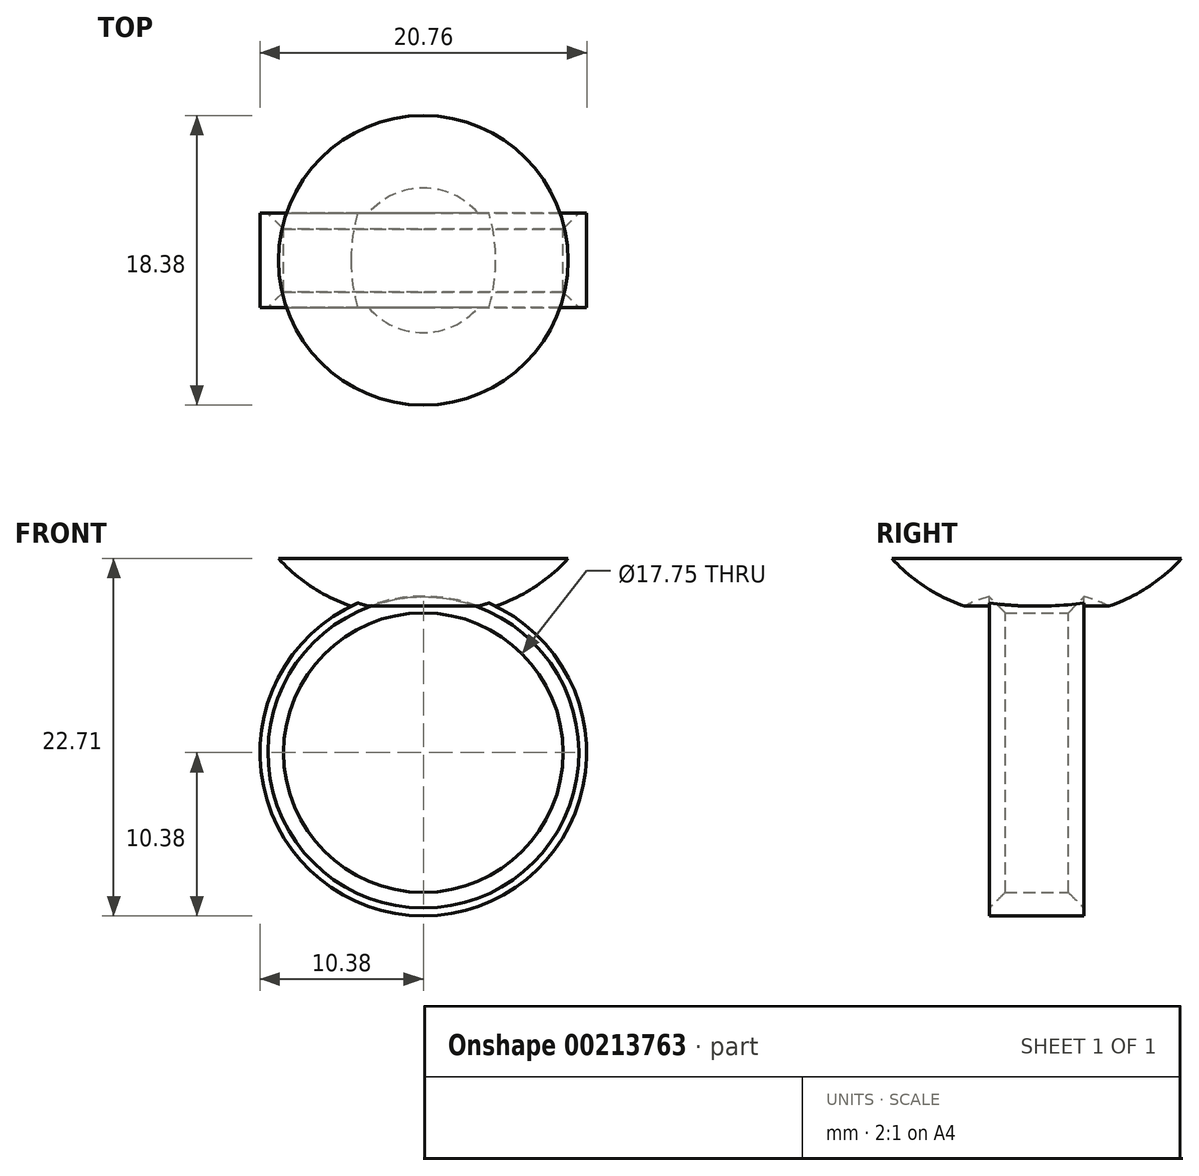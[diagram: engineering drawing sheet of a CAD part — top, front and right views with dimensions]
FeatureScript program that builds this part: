
annotation { "Feature Type Name" : "Feature", "Feature Type Description" : "" }
export const myFeature = defineFeature(function(context is Context, id is Id, definition is map)
    precondition{}
    {
        {
            var Q0;
            Q0=qCreatedBy(makeId("Front.planeOp"),FACE);
            var sketch = newSketch(context, id + "F0", { "sketchPlane" : qUnion([Q0])});
            skCircle(sketch, "E0", {"center": v(0, 0) * mm, "radius": 8.88 * mm});
            skCircle(sketch, "E1.0", {"center": v(0, 0) * mm, "radius": 10.38 * mm});
            skLineSegment(sketch, "E2", {"start": v(0, 9.3) * mm, "end": v(4.6, 9.3) * mm});
            skArc(sketch, "E3", {"start": v(4.6, 9.3) * mm, "mid": v(7.08, 10.53) * mm, "end": v(9.2, 12.33) * mm});
            skLineSegment(sketch, "E4", {"start": v(8.79, 13.33) * mm, "end": v(2.85, 27.83) * mm});
            skLineSegment(sketch, "E5", {"start": v(2.85, 27.83) * mm, "end": v(0, 27.83) * mm});
            skPoint(sketch, "E6", {"position": v(0, 9.3) * mm});
            skPoint(sketch, "E7.orphan", {"position": v(-4.6, 9.3) * mm});
            skLineSegment(sketch, "E8", {"start": v(0, 27.83) * mm, "end": v(0, 13.33) * mm});
            skLineSegment(sketch, "E9", {"start": v(9.2, 12.33) * mm, "end": v(0, 12.33) * mm});
            skPoint(sketch, "E10", {"position": v(0, 13.33) * mm});
            skLineSegment(sketch, "E11", {"start": v(0, 13.33) * mm, "end": v(8.79, 13.33) * mm});
            skLineSegment(sketch, "E12", {"start": v(0, 16.33) * mm, "end": v(3.5, 16.33) * mm});
            skLineSegment(sketch, "E13", {"start": v(3.5, 16.33) * mm, "end": v(3.5, 14.33) * mm});
            skLineSegment(sketch, "E14", {"start": v(3.5, 14.33) * mm, "end": v(1.5, 14.33) * mm});
            skLineSegment(sketch, "E15", {"start": v(1.5, 14.33) * mm, "end": v(1.5, 13.33) * mm});
            skLineSegment(sketch, "E16.trimOffspring", {"start": v(0, 12.33) * mm, "end": v(0, 9.3) * mm});
            skSolve(sketch);
        }
        {
            var Q0;
            Q0=qCreatedBy(makeId("Top.planeOp"),FACE);
            var sketch = newSketch(context, id + "F1", { "sketchPlane" : qUnion([Q0])});
            skCircle(sketch, "E17", {"center": v(0, 0) * mm, "radius": 4.62 * mm});
            skSolve(sketch);
        }
        {
            var Q0;
            {var subQ1=sQuery(id+"F0.wireOp",EDGE,"E3");Q0=makeQuery(id+"F0.imprint","IMPRINT",FACE,{"disambiguationData":[TD([[makeQuery(id+"F0.imprint","IMPRINT",EDGE,{"derivedFrom":subQ1}),1.0]])]});}
            var Q1;
            Q1=sQuery(id+"F1.wireOp",EDGE,"E17");
            revolve(context, id + "F2", {"entities" : qUnion([Q0]), "axis" : qUnion([Q1]), "revolveType" : RevolveType.FULL});
        }
        {
            var Q0;
            Q0=makeQuery(id+"F0.imprint","IMPRINT",FACE,{"disambiguationData":[TD([[makeQuery(id+"F0.imprint","IMPRINT",EDGE,{"derivedFrom":sQuery(id+"F0.wireOp",EDGE,"E0")}),-1.0]])]});
            var Q1;
            {var subQ0=sQuery(id+"F0.wireOp",EDGE,"E2");Q1=makeQuery(id+"F0.imprint","IMPRINT",FACE,{"disambiguationData":[TD([[makeQuery(id+"F0.imprint","IMPRINT",EDGE,{"derivedFrom":subQ0}),1.0]])]});}
            extrude(context, id + "F3", {"entities" : qUnion([Q0, Q1]), "operationType" : NewBodyOperationType.ADD, "depth" : 3 * mm, "hasSecondDirection" : true, "secondDirectionOppositeDirection" : true, "secondDirectionDepth" : 3 * mm});
        }
        {
            var Q0;
            Q0=makeQuery(id+"F3.opExtrude","CAP_EDGE",EDGE,{"disambiguationData":[OSD([sQuery(id+"F0.wireOp",EDGE,"E0")])],"isStart":false});
            var Q1;
            Q1=makeQuery(id+"F3.opExtrude","CAP_EDGE",EDGE,{"disambiguationData":[OSD([sQuery(id+"F0.wireOp",EDGE,"E0")])],"isStart":true});
            chamfer(context, id + "F4", {"entities" : qUnion([Q0, Q1]), "width" : 1 * mm, "tangentPropagation" : true});
        }
    });
